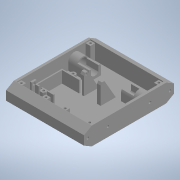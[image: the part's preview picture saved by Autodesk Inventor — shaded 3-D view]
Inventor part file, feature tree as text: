
AUTODESK INVENTOR PART (.ipt)
format: ipt  version: 2020 (Build 240168000, 168)  size: 587,776 bytes
history: native  units: in
note: dims shown in document units (in); Inventor stores cm internally (conversion verified against a paired STEP export)
features: extrude x17, sketch x16, projected_geometry x14, mirror x6, plane x1
ambient origin geometry x8: Origin, YZ Plane, XZ Plane, XY Plane, X Axis, Y Axis, Z Axis, Center Point
bodies: Solid1 (feature_tree)
feature tree (54):
  extrude  "Extrusion1"  Depth=5.9055in
  extrude  "Extrusion2"  TaperAngle=0.0deg  [1 undecoded]
  extrude  "Extrusion3"  Depth=1.063in
  extrude  "Extrusion4"  Depth=0.315in
  extrude  "Extrusion5"  TaperAngle=0.0deg  [1 undecoded]
  extrude  "Extrusion6"  Depth=0.5906in
  mirror  "Mirror1"
  extrude  "Extrusion7"  Depth=0.0787in
  mirror  "Mirror2"
  extrude  "Extrusion8"  Depth=0.6102in
  mirror  "Mirror3"
  plane  "Work Plane1"
  extrude  "Extrusion9"  Depth=0.7874in TaperAngle=0.0deg
  mirror  "Mirror4"
  extrude  "Extrusion10"  Depth=6.063in TaperAngle=0.0deg
  extrude  "Extrusion11"  Depth=0.1575in
  extrude  "Extrusion12"  TaperAngle=0.0deg  [1 undecoded]
  extrude  "Extrusion13"  Depth=0.2756in
  extrude  "Extrusion14"  Depth=0.4331in
  extrude  "Extrusion17"  Depth=2.7559in
  extrude  "Extrusion18"  Depth=0.0394in
  mirror  "Mirror6"
  extrude  "Extrusion19"  Depth=0.2362in
  mirror  "Mirror7"
  sketch  "Sketch1"  dims[d0=1.1811in d1=5.9055in]
  sketch  "Sketch2"  dims[d2=5.1181in d3=0.0in]
  projected_geometry  "Projected Loop1"
  sketch  "Sketch3"  dims[d4=0.1575in d5=1.063in]
  projected_geometry  "Projected Loop2"
  projected_geometry  "Projected Loop3"
  sketch  "Sketch4"  dims[d6=0.0in d8=0.315in]
  projected_geometry  "Projected Loop4"
  sketch  "Sketch6"  dims[d10=0.993in d11=0.0in]
  sketch  "Sketch7"  dims[d12=0.6496in d13=0.5906in]
  sketch  "Sketch9"  dims[d14=1.5748in d15=0.0787in]
  sketch  "Sketch10"  dims[d16=0.5512in d17=0.0in d18=0.6102in]
  sketch  "Sketch12"  dims[d19=0.4803in d20=0.7874in d21=0.0in]
  projected_geometry  "Projected Loop6"
  projected_geometry  "Projected Loop7"
  projected_geometry  "Projected Loop8"
  sketch  "Sketch13"  dims[d22=0.1654in d23=6.063in d24=0.0in]
  sketch  "Sketch14"  dims[d25=0.5114in d26=0.1575in]
  sketch  "Sketch15"  dims[d27=1.5748in d28=0.0in d29=0.0in]
  projected_geometry  "Projected Loop15"
  sketch  "Sketch16"  dims[d30=0.1575in d31=0.2756in]
  projected_geometry  "Projected Loop19"
  projected_geometry  "Projected Loop20"
  projected_geometry  "Projected Loop21"
  projected_geometry  "Projected Loop22"
  projected_geometry  "Projected Loop23"
  projected_geometry  "Projected Loop24"
  sketch  "Sketch20"  dims[d32=0.0in d33=0.4331in]
  sketch  "Sketch21"  dims[d34=0.122in d38=2.7559in]
  sketch  "Sketch22"  dims[d40=0.061in d41=0.0909in d42=0.2362in d43=0.0in d44=60.0deg d45=0.0787in d46=0.315in d48=0.993in d49=0.0in d53=0.2756in d54=0.0in d55=0.4724in d56=1.2008in d57=1.6142in d58=1.5945in d59=0.0787in d60=0.0787in d62=0.315in d63=0.7677in d64=0.0in d66=0.1476in d67=0.2756in d68=0.0in d69=0.8268in d70=0.2953in d71=0.1181in d72=0.0in d89=0.0157in d90=0.0157in d91=0.1476in d92=0.1476in d96=0.315in d97=0.1575in d98=0.1181in d99=0.0in d102=0.1772in d104=0.3346in d105=135.0deg d106=0.2362in d107=0.0in d108=0.0394in d109=0.0in]
note: 3 required parameter values undecoded (feature->parameter linkage not recoverable at this tier; creation-order binding heuristic only, values carry confidence <= 0.55)
